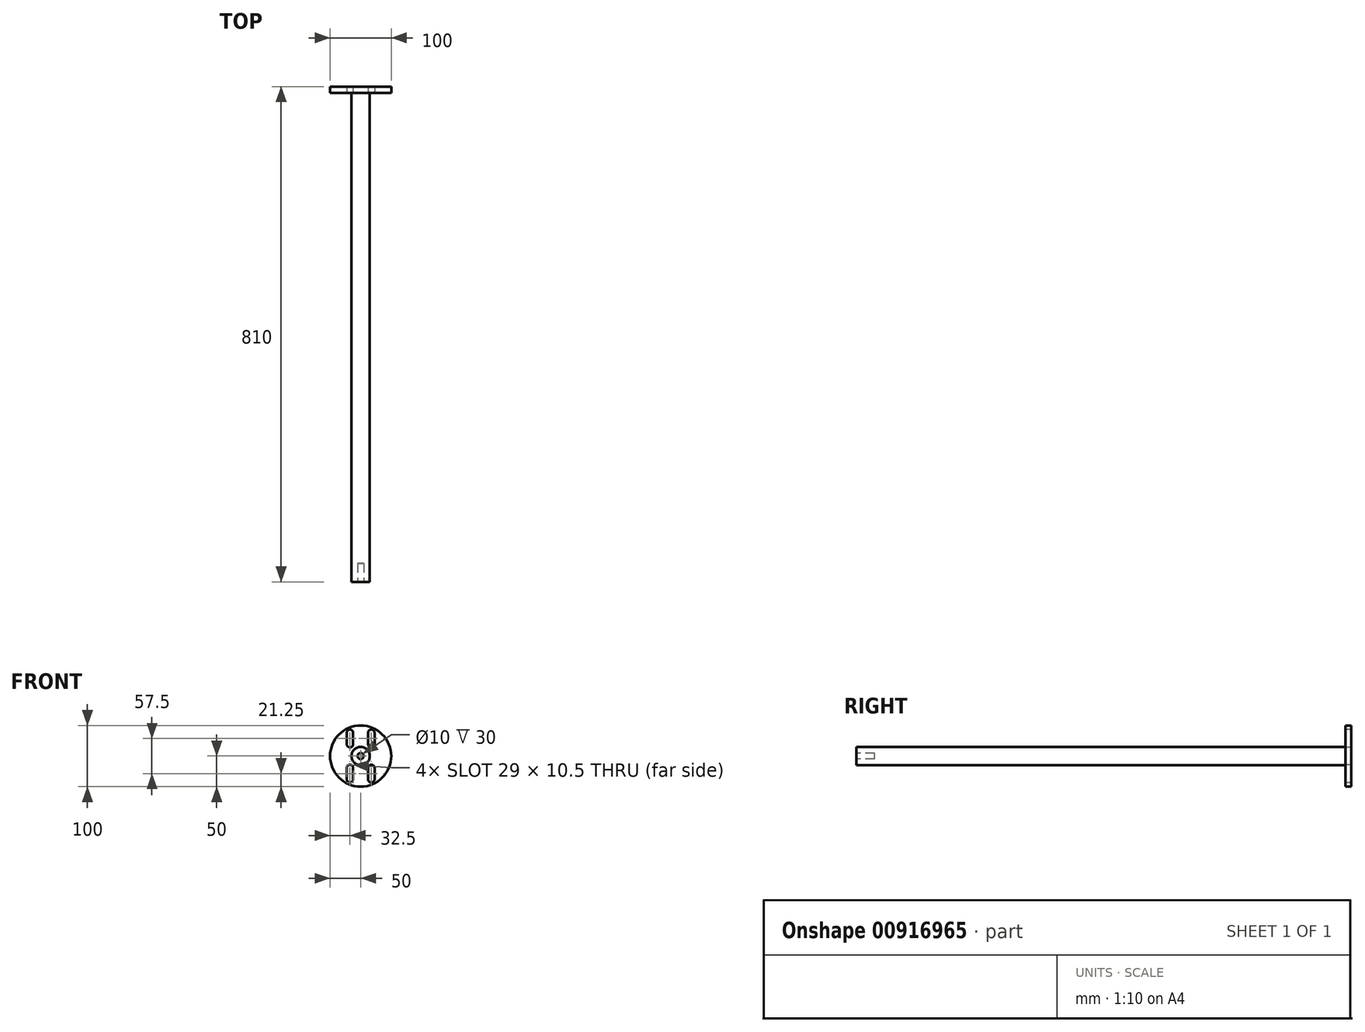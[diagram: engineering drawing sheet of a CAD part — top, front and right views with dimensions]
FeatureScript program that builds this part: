
annotation { "Feature Type Name" : "Feature", "Feature Type Description" : "" }
export const myFeature = defineFeature(function(context is Context, id is Id, definition is map)
    precondition{}
    {
        {
            var Q0;
            Q0=qCreatedBy(makeId("Front.planeOp"),FACE);
            var sketch = newSketch(context, id + "F0", { "sketchPlane" : qUnion([Q0])});
            skCircle(sketch, "E0", {"center": v(0, 0) * mm, "radius": 15 * mm});
            skSolve(sketch);
        }
        {
            var Q0;
            Q0=makeQuery(id+"F0.imprint","IMPRINT",FACE,{"disambiguationData":[TD([[makeQuery(id+"F0.imprint","IMPRINT",EDGE,{"derivedFrom":sQuery(id+"F0.wireOp",EDGE,"E0")}),1.0]])]});
            extrude(context, id + "F1", {"entities" : qUnion([Q0]), "depth" : 800 * mm, "offsetDistance" : 25 * mm});
        }
        {
            var Q0;
            Q0=makeQuery(id+"F1.opExtrude","CAP_FACE",FACE,{"disambiguationData":[OSD([sQuery(id+"F0.wireOp",EDGE,"E0")])],"isStart":true});
            var sketch = newSketch(context, id + "F2", { "sketchPlane" : qUnion([Q0])});
            skCircle(sketch, "E1", {"center": v(0, 0) * mm, "radius": 50 * mm});
            skLineSegment(sketch, "E2.bottom", {"start": v(-17.5, 43.25) * mm, "end": v(-17.5, 43.25) * mm});
            skLineSegment(sketch, "E2.top", {"start": v(-17.5, 14.25) * mm, "end": v(-17.5, 14.25) * mm});
            skLineSegment(sketch, "E2.left", {"start": v(-22.75, 38) * mm, "end": v(-22.75, 19.5) * mm});
            skLineSegment(sketch, "E2.right", {"start": v(-12.25, 38) * mm, "end": v(-12.25, 19.5) * mm});
            skPoint(sketch, "E3.visualSharp", {"position": v(-22.75, 43.25) * mm});
            skArc(sketch, "E3.filletArc", {"start": v(-17.5, 43.25) * mm, "mid": v(-21.21, 41.71) * mm, "end": v(-22.75, 38) * mm});
            skPoint(sketch, "E4.visualSharp", {"position": v(-12.25, 43.25) * mm});
            skArc(sketch, "E4.filletArc", {"start": v(-12.25, 38) * mm, "mid": v(-13.79, 41.71) * mm, "end": v(-17.5, 43.25) * mm});
            skPoint(sketch, "E5.visualSharp", {"position": v(-12.25, 14.25) * mm});
            skArc(sketch, "E5.filletArc", {"start": v(-17.5, 14.25) * mm, "mid": v(-13.79, 15.79) * mm, "end": v(-12.25, 19.5) * mm});
            skPoint(sketch, "E6.visualSharp", {"position": v(-22.75, 14.25) * mm});
            skArc(sketch, "E6.filletArc", {"start": v(-22.75, 19.5) * mm, "mid": v(-21.21, 15.79) * mm, "end": v(-17.5, 14.25) * mm});
            skLineSegment(sketch, "E7.0.1.0", {"start": v(-12.25, -19.5) * mm, "end": v(-12.25, -38) * mm});
            skLineSegment(sketch, "E7.0.1.1", {"start": v(-22.75, -19.5) * mm, "end": v(-22.75, -38) * mm});
            skArc(sketch, "E7.0.1.2", {"start": v(-17.5, -14.25) * mm, "mid": v(-21.21, -15.79) * mm, "end": v(-22.75, -19.5) * mm});
            skArc(sketch, "E7.0.1.3", {"start": v(-12.25, -19.5) * mm, "mid": v(-13.79, -15.79) * mm, "end": v(-17.5, -14.25) * mm});
            skArc(sketch, "E7.0.1.4", {"start": v(-17.5, -43.25) * mm, "mid": v(-13.79, -41.71) * mm, "end": v(-12.25, -38) * mm});
            skArc(sketch, "E7.0.1.5", {"start": v(-22.75, -38) * mm, "mid": v(-21.21, -41.71) * mm, "end": v(-17.5, -43.25) * mm});
            skLineSegment(sketch, "E7.1.0.0", {"start": v(22.75, 38) * mm, "end": v(22.75, 19.5) * mm});
            skLineSegment(sketch, "E7.1.0.1", {"start": v(12.25, 38) * mm, "end": v(12.25, 19.5) * mm});
            skArc(sketch, "E7.1.0.2", {"start": v(17.5, 43.25) * mm, "mid": v(13.79, 41.71) * mm, "end": v(12.25, 38) * mm});
            skArc(sketch, "E7.1.0.3", {"start": v(22.75, 38) * mm, "mid": v(21.21, 41.71) * mm, "end": v(17.5, 43.25) * mm});
            skArc(sketch, "E7.1.0.4", {"start": v(17.5, 14.25) * mm, "mid": v(21.21, 15.79) * mm, "end": v(22.75, 19.5) * mm});
            skArc(sketch, "E7.1.0.5", {"start": v(12.25, 19.5) * mm, "mid": v(13.79, 15.79) * mm, "end": v(17.5, 14.25) * mm});
            skLineSegment(sketch, "E7.1.1.0", {"start": v(22.75, -19.5) * mm, "end": v(22.75, -38) * mm});
            skLineSegment(sketch, "E7.1.1.1", {"start": v(12.25, -19.5) * mm, "end": v(12.25, -38) * mm});
            skArc(sketch, "E7.1.1.2", {"start": v(17.5, -14.25) * mm, "mid": v(13.79, -15.79) * mm, "end": v(12.25, -19.5) * mm});
            skArc(sketch, "E7.1.1.3", {"start": v(22.75, -19.5) * mm, "mid": v(21.21, -15.79) * mm, "end": v(17.5, -14.25) * mm});
            skArc(sketch, "E7.1.1.4", {"start": v(17.5, -43.25) * mm, "mid": v(21.21, -41.71) * mm, "end": v(22.75, -38) * mm});
            skArc(sketch, "E7.1.1.5", {"start": v(12.25, -38) * mm, "mid": v(13.79, -41.71) * mm, "end": v(17.5, -43.25) * mm});
            skLineSegment(sketch, "E7.direction1", {"start": v(-12.25, 19.5) * mm, "end": v(22.75, 19.5) * mm, "construction": true});
            skLineSegment(sketch, "E7.direction2", {"start": v(-12.25, 19.5) * mm, "end": v(-12.25, -38) * mm, "construction": true});
            skSolve(sketch);
        }
        {
            var Q0;
            Q0 = qSketchRegion(id + "F2", true);
            extrude(context, id + "F3", {"entities" : qUnion([Q0]), "operationType" : NewBodyOperationType.ADD, "depth" : 10 * mm, "offsetDistance" : 25 * mm});
        }
        {
            var Q0;
            Q0=makeQuery(id+"F1.opExtrude","CAP_FACE",FACE,{"disambiguationData":[OSD([sQuery(id+"F0.wireOp",EDGE,"E0")])],"isStart":false});
            var sketch = newSketch(context, id + "F4", { "sketchPlane" : qUnion([Q0])});
            skCircle(sketch, "E8", {"center": v(0, 0) * mm, "radius": 5 * mm});
            skSolve(sketch);
        }
        {
            var Q0;
            Q0=makeQuery(id+"F4.imprint","IMPRINT",FACE,{"disambiguationData":[TD([[makeQuery(id+"F4.imprint","IMPRINT",EDGE,{"derivedFrom":sQuery(id+"F4.wireOp",EDGE,"E8")}),1.0]])]});
            extrude(context, id + "F5", {"entities" : qUnion([Q0]), "operationType" : NewBodyOperationType.REMOVE, "oppositeDirection" : true, "depth" : 30 * mm, "offsetDistance" : 25 * mm});
        }
    });
